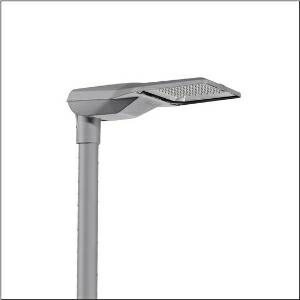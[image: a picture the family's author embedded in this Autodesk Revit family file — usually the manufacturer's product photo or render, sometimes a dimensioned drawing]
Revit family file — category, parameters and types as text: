
# Revit family: streetlight_sl_21_iq_midi___st1_5a_5xe3p31g08mb_98ff
name_source: partatom
category: Lighting Fixtures
units: mm (PartAtom-declared; Revit-internal decimal feet)

## family parameters
Cut with Voids When Loaded = No
Host = Face
Light Source = No
Part Type = Normal
Room Calculation Point = No
Round Connector Dimension = Use Diameter
Shared = No

## types (1)
- --- (1 x LED, 19170 lm, 146.7 W, 3000K)
    Apparent Load = 147 VA
    CIE Flux Codes = 22 53 95 100 100
    Color Rendering = 70
    Color Temperature = 3000K
    Default Elevation = 1800 mm
    Description = Streetlight SL 21 iQ midi, mast luminaire, primary light control with lens, of PMMA, primary optical cover: cover, of toughened safety glass, transparent, light distribution: ST1.5a, light emission: direct distribution, primary light characteristic: asymmetric, installation type: post-top, side-entry, LED, High Power LED, rated luminous flux: 19.170lm, luminous efficacy: 131lm/W, light colour: 730, colour temperature: 3000K, control gear: iQ Street-Remote, control: Street-Remote, Auto-Match, Temp-Guard, Lumen-Switch, Night-Set, Smart-Wire, Light-Fading, Desk-Remote (wireless, voltage-free reading and setting of iQ features in the workshop via application-optimized NFC function/RFID function), optimised constant luminous flux control (CLO 2.0), pre-setting: linear dimming characteristic, mains connection: 230..240V, AC, 50/60Hz, start of lifetime: 147W, end of service life: 161W, reduction: 62W, luminaire housing, of diecast aluminium, powder-coated, Siteco® metallic grey (DB 702S), corrosivity category C5 mid according to DIN EN ISO 12944, please order mast flange separately, inclination adjustable: 0°, 5°, 10°, 15°, sealing non-destructively replaceable, multi-level sealing system, length: 644mm, width: 335mm, height: 110mm, mast flange for spigot size: 42mm (side-entry): 5XC10008XM4, 60/48mm (side-entry/post-top): 5XC10108XM2, 76/60mm (side-entry/post-top): 5XC10108XM1, mounting height: 4..8m, protection rating (complete): IP66, insulation class (complete): insulation class II (safety insulation), certification: CE, ENEC, ENEC+, VDE, impact resistance: IK10, permissible operating ambient temperature for outdoor applications: -40..+50°C, standard-compliant lighting for roads and squares, packaging unit: 1 piece

Light Distribution: ST1.5a
    Height = 111 mm
    Lamp = 1 x LED
    Lamp Light Flux = 19170 lm
    Lamp Power = 146.7 W
    Lamp count = 1
    Length = 644 mm
    Luminous efficacy = 131 lm/W
    Manufacturer = Siteco
    ModVariant = No
    Model = 5XE3P31G08MB
    Number of Poles = 1
    OnlyDefault = Yes
    Power Factor = 1
    Product Name = Streetlight SL 21 iQ midi | ST1.5a
    Product group = mast luminaire | pylon top
    ProductGroupID = 6100
    Protection Class = Protection class II
    Protection Degree = IP 66
    RLX_Detail_Level = 1
    RLX_Emergency_Light_Flux = 0 lm
    RLX_Emergency_Type = 0
    RLX_Emergency_Type_DB = No
    RlxData = <blob elided: 30501 chars, md5=69c5284a>
    Socket = socket
    Standby Power = 0 W
    System Light Flux = 19169 lm
    System Power = 147 W
    Type Comments = factory setting: luminous flux: 100 % | dim-lin: 254 | 753 mA
    Type Image = l_1004298.jpg
    URL = http://relux.com
    VarID = @adj_197761
    Voltage = 0 V
    Weight = 0.00 kg
    Width = 336 mm

## geometry (parser evidence)
native form markers: Blend x4, Sweep x11
no freeform markers — native parametric forms only
